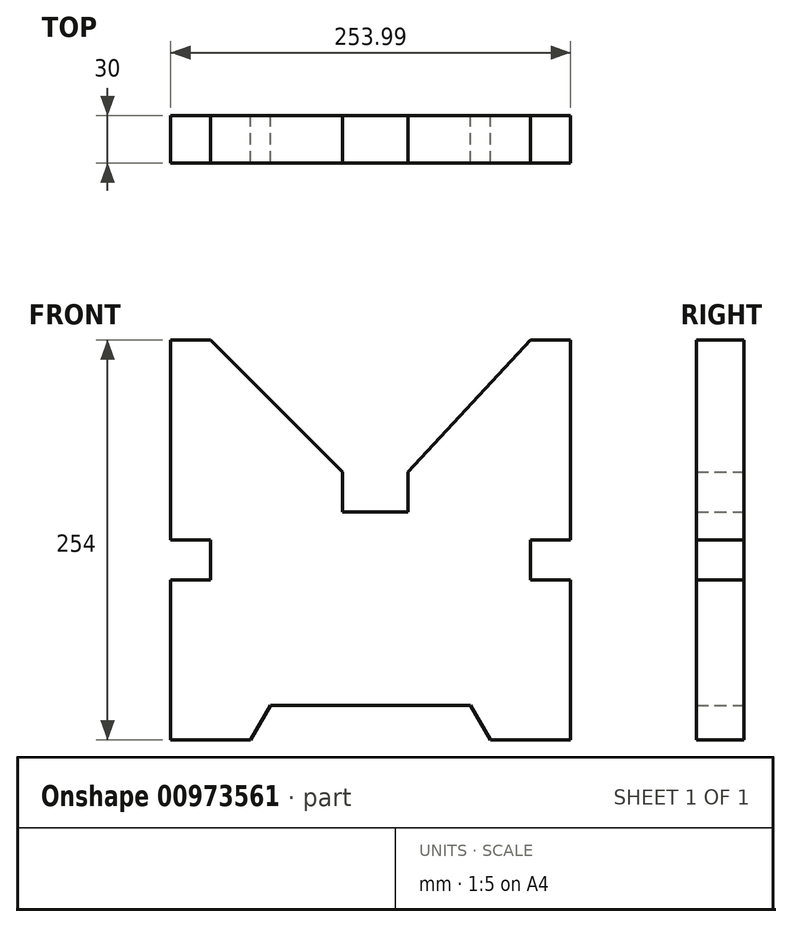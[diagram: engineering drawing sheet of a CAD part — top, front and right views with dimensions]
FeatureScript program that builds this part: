
annotation { "Feature Type Name" : "Feature", "Feature Type Description" : "" }
export const myFeature = defineFeature(function(context is Context, id is Id, definition is map)
    precondition{}
    {
        {
            var Q0;
            Q0=qCreatedBy(makeId("Front.planeOp"),FACE);
            var sketch = newSketch(context, id + "F0", { "sketchPlane" : qUnion([Q0])});
            skLineSegment(sketch, "E0", {"start": v(-149.75, 137.97) * mm, "end": v(-124.35, 137.97) * mm});
            skLineSegment(sketch, "E1", {"start": v(-149.75, 137.97) * mm, "end": v(-149.75, 10.97) * mm});
            skLineSegment(sketch, "E2", {"start": v(-149.75, 10.97) * mm, "end": v(-124.35, 10.97) * mm});
            skLineSegment(sketch, "E3", {"start": v(-124.35, 10.97) * mm, "end": v(-124.35, -14.43) * mm});
            skLineSegment(sketch, "E4", {"start": v(-124.35, -14.43) * mm, "end": v(-149.75, -14.43) * mm});
            skLineSegment(sketch, "E5", {"start": v(-149.75, -14.43) * mm, "end": v(-149.75, -116.03) * mm});
            skLineSegment(sketch, "E6", {"start": v(1.14, 54.14) * mm, "end": v(78.84, 137.97) * mm});
            skLineSegment(sketch, "E7", {"start": v(78.84, 137.97) * mm, "end": v(104.24, 137.97) * mm});
            skLineSegment(sketch, "E8", {"start": v(104.24, 137.97) * mm, "end": v(104.24, 10.97) * mm});
            skLineSegment(sketch, "E9", {"start": v(104.24, 10.97) * mm, "end": v(78.84, 10.97) * mm});
            skLineSegment(sketch, "E10", {"start": v(78.84, 10.97) * mm, "end": v(78.84, -14.43) * mm});
            skLineSegment(sketch, "E11", {"start": v(78.84, -14.43) * mm, "end": v(104.24, -14.43) * mm});
            skLineSegment(sketch, "E12", {"start": v(104.24, -14.43) * mm, "end": v(104.24, -116.03) * mm});
            skLineSegment(sketch, "E13", {"start": v(-149.75, -116.03) * mm, "end": v(-98.95, -116.03) * mm});
            skLineSegment(sketch, "E14", {"start": v(-98.95, -116.03) * mm, "end": v(-86.26, -94.03) * mm});
            skLineSegment(sketch, "E15", {"start": v(-124.35, 137.97) * mm, "end": v(-40.52, 54.14) * mm});
            skLineSegment(sketch, "E16", {"start": v(-40.52, 54.14) * mm, "end": v(-40.52, 28.74) * mm});
            skLineSegment(sketch, "E17", {"start": v(-40.52, 28.74) * mm, "end": v(1.14, 28.74) * mm});
            skLineSegment(sketch, "E18", {"start": v(1.14, 28.74) * mm, "end": v(1.14, 54.14) * mm});
            skLineSegment(sketch, "E19", {"start": v(-86.26, -94.03) * mm, "end": v(40.74, -94.03) * mm});
            skLineSegment(sketch, "E20", {"start": v(40.74, -94.03) * mm, "end": v(53.44, -116.02) * mm});
            skLineSegment(sketch, "E21", {"start": v(53.44, -116.02) * mm, "end": v(104.24, -116.03) * mm});
            skSolve(sketch);
        }
        {
            var Q0;
            Q0 = qSketchRegion(id + "F0", true);
            extrude(context, id + "F1", {"entities" : qUnion([Q0]), "depth" : 30 * mm, "offsetDistance" : 25.4 * mm});
        }
    });
